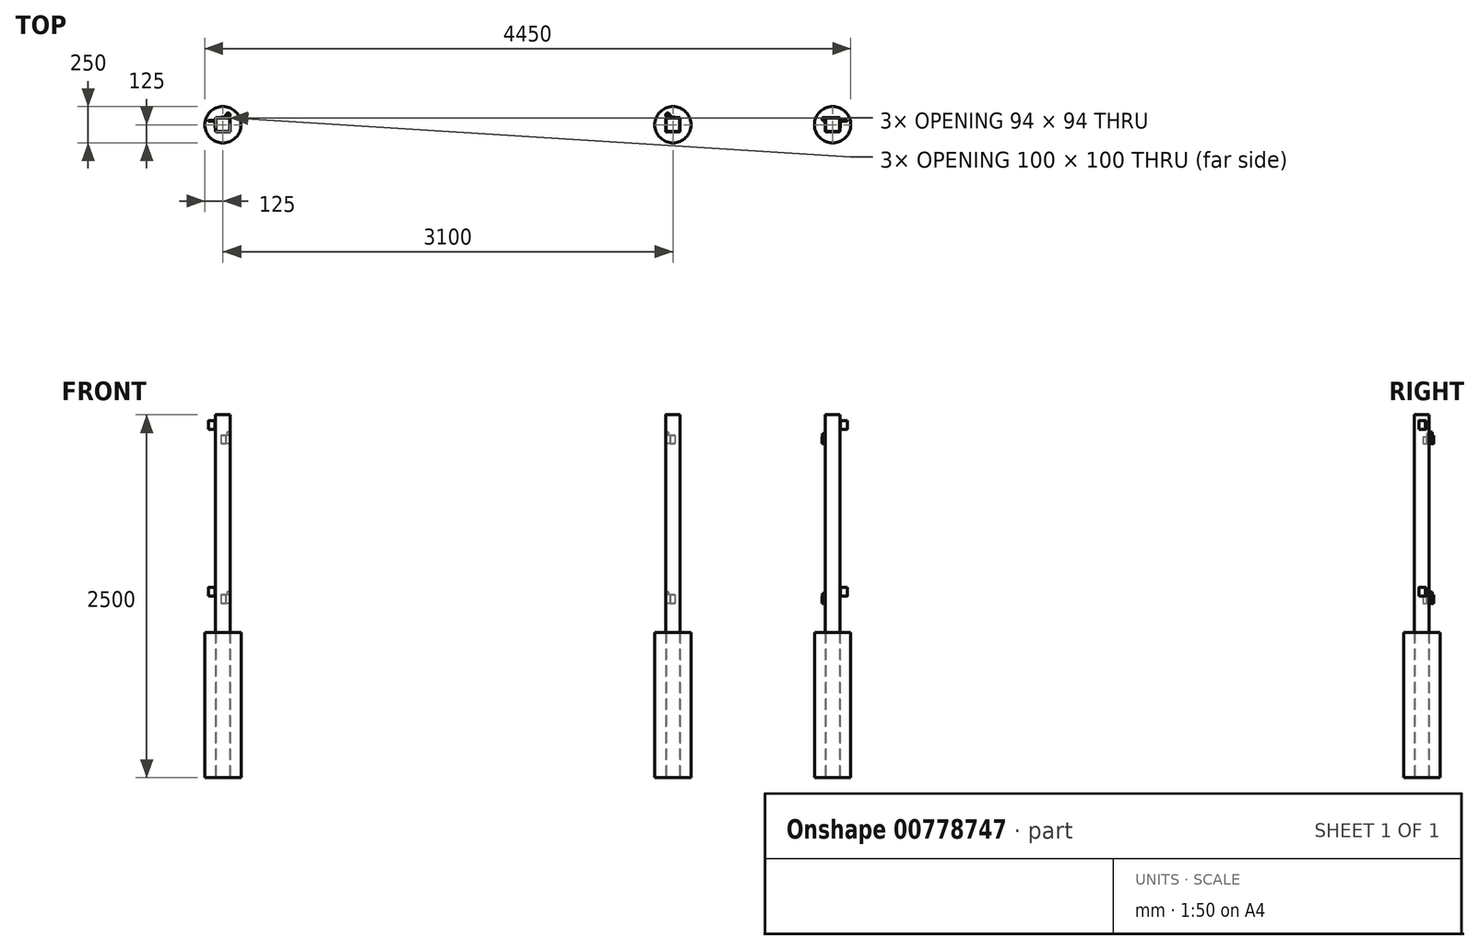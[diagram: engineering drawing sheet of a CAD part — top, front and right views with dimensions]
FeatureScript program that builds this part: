
annotation { "Feature Type Name" : "Feature", "Feature Type Description" : "" }
export const myFeature = defineFeature(function(context is Context, id is Id, definition is map)
    precondition{}
    {
        {
            var Q0;
            Q0=qCreatedBy(makeId("Top.planeOp"),FACE);
            cPlane(context, id + "F0", {"entities" : qUnion([Q0]), "cplaneType" : CPlaneType.OFFSET, "offset" : 1000 * mm, "oppositeDirection" : true, "width" : 150 * mm, "height" : 150 * mm});
        }
        {
            var Q0;
            Q0=qCreatedBy(id+"F0.planeOp",FACE);
            var sketch = newSketch(context, id + "F1", { "sketchPlane" : qUnion([Q0])});
            skLineSegment(sketch, "E0.bottom", {"start": v(-1594, 50) * mm, "end": v(-1506, 50) * mm});
            skLineSegment(sketch, "E0.top", {"start": v(-1594, -50) * mm, "end": v(-1506, -50) * mm});
            skLineSegment(sketch, "E0.left", {"start": v(-1600, 44) * mm, "end": v(-1600, -44) * mm});
            skLineSegment(sketch, "E0.right", {"start": v(-1500, 44) * mm, "end": v(-1500, -44) * mm});
            skLineSegment(sketch, "E1.bottom", {"start": v(1506, 50) * mm, "end": v(1594, 50) * mm});
            skLineSegment(sketch, "E1.top", {"start": v(1506, -50) * mm, "end": v(1594, -50) * mm});
            skLineSegment(sketch, "E1.left", {"start": v(1500, 44) * mm, "end": v(1500, -44) * mm});
            skLineSegment(sketch, "E1.right", {"start": v(1600, 44) * mm, "end": v(1600, -44) * mm});
            skLineSegment(sketch, "E2.bottom", {"start": v(2606, 50) * mm, "end": v(2694, 50) * mm});
            skLineSegment(sketch, "E2.top", {"start": v(2606, -50) * mm, "end": v(2694, -50) * mm});
            skLineSegment(sketch, "E2.left", {"start": v(2600, 44) * mm, "end": v(2600, -44) * mm});
            skLineSegment(sketch, "E2.right", {"start": v(2700, 44) * mm, "end": v(2700, -44) * mm});
            skPoint(sketch, "E3.visualSharp", {"position": v(-1600, 50) * mm});
            skArc(sketch, "E3.filletArc", {"start": v(-1594, 50) * mm, "mid": v(-1598.24, 48.24) * mm, "end": v(-1600, 44) * mm});
            skPoint(sketch, "E4.visualSharp", {"position": v(-1500, 50) * mm});
            skArc(sketch, "E4.filletArc", {"start": v(-1500, 44) * mm, "mid": v(-1501.76, 48.24) * mm, "end": v(-1506, 50) * mm});
            skPoint(sketch, "E5.visualSharp", {"position": v(-1500, -50) * mm});
            skArc(sketch, "E5.filletArc", {"start": v(-1506, -50) * mm, "mid": v(-1501.76, -48.24) * mm, "end": v(-1500, -44) * mm});
            skPoint(sketch, "E6.visualSharp", {"position": v(-1600, -50) * mm});
            skArc(sketch, "E6.filletArc", {"start": v(-1600, -44) * mm, "mid": v(-1598.24, -48.24) * mm, "end": v(-1594, -50) * mm});
            skPoint(sketch, "E7.visualSharp", {"position": v(1500, 50) * mm});
            skArc(sketch, "E7.filletArc", {"start": v(1506, 50) * mm, "mid": v(1501.76, 48.24) * mm, "end": v(1500, 44) * mm});
            skPoint(sketch, "E8.visualSharp", {"position": v(1600, 50) * mm});
            skArc(sketch, "E8.filletArc", {"start": v(1600, 44) * mm, "mid": v(1598.24, 48.24) * mm, "end": v(1594, 50) * mm});
            skPoint(sketch, "E9.visualSharp", {"position": v(1600, -50) * mm});
            skArc(sketch, "E9.filletArc", {"start": v(1594, -50) * mm, "mid": v(1598.24, -48.24) * mm, "end": v(1600, -44) * mm});
            skPoint(sketch, "E10.visualSharp", {"position": v(1500, -50) * mm});
            skArc(sketch, "E10.filletArc", {"start": v(1500, -44) * mm, "mid": v(1501.76, -48.24) * mm, "end": v(1506, -50) * mm});
            skPoint(sketch, "E11.visualSharp", {"position": v(2600, 50) * mm});
            skArc(sketch, "E11.filletArc", {"start": v(2606, 50) * mm, "mid": v(2601.76, 48.24) * mm, "end": v(2600, 44) * mm});
            skPoint(sketch, "E12.visualSharp", {"position": v(2700, 50) * mm});
            skArc(sketch, "E12.filletArc", {"start": v(2700, 44) * mm, "mid": v(2698.24, 48.24) * mm, "end": v(2694, 50) * mm});
            skPoint(sketch, "E13.visualSharp", {"position": v(2700, -50) * mm});
            skArc(sketch, "E13.filletArc", {"start": v(2694, -50) * mm, "mid": v(2698.24, -48.24) * mm, "end": v(2700, -44) * mm});
            skPoint(sketch, "E14.visualSharp", {"position": v(2600, -50) * mm});
            skArc(sketch, "E14.filletArc", {"start": v(2600, -44) * mm, "mid": v(2601.76, -48.24) * mm, "end": v(2606, -50) * mm});
            skArc(sketch, "E15.0", {"start": v(-1594, 47) * mm, "mid": v(-1596.12, 46.12) * mm, "end": v(-1597, 44) * mm});
            skLineSegment(sketch, "E15.1", {"start": v(-1594, 47) * mm, "end": v(-1506, 47) * mm});
            skLineSegment(sketch, "E15.2", {"start": v(-1597, 44) * mm, "end": v(-1597, -44) * mm});
            skArc(sketch, "E15.3", {"start": v(-1503, 44) * mm, "mid": v(-1503.88, 46.12) * mm, "end": v(-1506, 47) * mm});
            skArc(sketch, "E15.4", {"start": v(-1597, -44) * mm, "mid": v(-1596.12, -46.12) * mm, "end": v(-1594, -47) * mm});
            skLineSegment(sketch, "E15.5", {"start": v(-1594, -47) * mm, "end": v(-1506, -47) * mm});
            skArc(sketch, "E15.6", {"start": v(-1506, -47) * mm, "mid": v(-1503.88, -46.12) * mm, "end": v(-1503, -44) * mm});
            skLineSegment(sketch, "E15.7", {"start": v(-1503, 44) * mm, "end": v(-1503, -44) * mm});
            skArc(sketch, "E16.0", {"start": v(1506, 47) * mm, "mid": v(1503.88, 46.12) * mm, "end": v(1503, 44) * mm});
            skLineSegment(sketch, "E16.1", {"start": v(1506, 47) * mm, "end": v(1594, 47) * mm});
            skLineSegment(sketch, "E16.2", {"start": v(1503, 44) * mm, "end": v(1503, -44) * mm});
            skArc(sketch, "E16.3", {"start": v(1597, 44) * mm, "mid": v(1596.12, 46.12) * mm, "end": v(1594, 47) * mm});
            skArc(sketch, "E16.4", {"start": v(1503, -44) * mm, "mid": v(1503.88, -46.12) * mm, "end": v(1506, -47) * mm});
            skLineSegment(sketch, "E16.5", {"start": v(1506, -47) * mm, "end": v(1594, -47) * mm});
            skArc(sketch, "E16.6", {"start": v(1594, -47) * mm, "mid": v(1596.12, -46.12) * mm, "end": v(1597, -44) * mm});
            skLineSegment(sketch, "E16.7", {"start": v(1597, 44) * mm, "end": v(1597, -44) * mm});
            skArc(sketch, "E17.0", {"start": v(2606, 47) * mm, "mid": v(2603.88, 46.12) * mm, "end": v(2603, 44) * mm});
            skLineSegment(sketch, "E17.1", {"start": v(2606, 47) * mm, "end": v(2694, 47) * mm});
            skLineSegment(sketch, "E17.2", {"start": v(2603, 44) * mm, "end": v(2603, -44) * mm});
            skArc(sketch, "E17.3", {"start": v(2697, 44) * mm, "mid": v(2696.12, 46.12) * mm, "end": v(2694, 47) * mm});
            skArc(sketch, "E17.4", {"start": v(2603, -44) * mm, "mid": v(2603.88, -46.12) * mm, "end": v(2606, -47) * mm});
            skLineSegment(sketch, "E17.5", {"start": v(2606, -47) * mm, "end": v(2694, -47) * mm});
            skArc(sketch, "E17.6", {"start": v(2694, -47) * mm, "mid": v(2696.12, -46.12) * mm, "end": v(2697, -44) * mm});
            skLineSegment(sketch, "E17.7", {"start": v(2697, 44) * mm, "end": v(2697, -44) * mm});
            skCircle(sketch, "E18", {"center": v(-1550, 0) * mm, "radius": 125 * mm});
            skPoint(sketch, "E18.centerSnap0", {"position": v(-1550, 47) * mm});
            skPoint(sketch, "E18.centerSnap1", {"position": v(-1500, 0) * mm});
            skCircle(sketch, "E19", {"center": v(1550, 0) * mm, "radius": 125 * mm});
            skPoint(sketch, "E19.centerSnap0", {"position": v(1597, 0) * mm});
            skPoint(sketch, "E19.centerSnap1", {"position": v(1550, 47) * mm});
            skCircle(sketch, "E20", {"center": v(2650, 0) * mm, "radius": 125 * mm});
            skPoint(sketch, "E20.centerSnap0", {"position": v(2697, 0) * mm});
            skPoint(sketch, "E20.centerSnap1", {"position": v(2650, 47) * mm});
            skSolve(sketch);
        }
        {
            var Q0;
            Q0=makeQuery(id+"F1.imprint","IMPRINT",FACE,{"disambiguationData":[TD([[makeQuery(id+"F1.imprint","IMPRINT",EDGE,{"derivedFrom":sQuery(id+"F1.wireOp",EDGE,"E0.bottom")}),-1.0]])]});
            var Q1;
            Q1=makeQuery(id+"F1.imprint","IMPRINT",FACE,{"disambiguationData":[TD([[makeQuery(id+"F1.imprint","IMPRINT",EDGE,{"derivedFrom":sQuery(id+"F1.wireOp",EDGE,"E1.bottom")}),-1.0]])]});
            var Q2;
            Q2=makeQuery(id+"F1.imprint","IMPRINT",FACE,{"disambiguationData":[TD([[makeQuery(id+"F1.imprint","IMPRINT",EDGE,{"derivedFrom":sQuery(id+"F1.wireOp",EDGE,"E2.bottom")}),-1.0]])]});
            extrude(context, id + "F2", {"entities" : qUnion([Q0, Q1, Q2]), "depth" : 2500 * mm, "offsetDistance" : 25 * mm});
        }
        {
            var Q0;
            Q0=makeQuery(id+"F1.imprint","IMPRINT",FACE,{"disambiguationData":[TD([[makeQuery(id+"F1.imprint","IMPRINT",EDGE,{"derivedFrom":sQuery(id+"F1.wireOp",EDGE,"E0.bottom")}),1.0]])]});
            var Q1;
            Q1=makeQuery(id+"F1.imprint","IMPRINT",FACE,{"disambiguationData":[TD([[makeQuery(id+"F1.imprint","IMPRINT",EDGE,{"derivedFrom":sQuery(id+"F1.wireOp",EDGE,"E1.bottom")}),1.0]])]});
            var Q2;
            Q2=makeQuery(id+"F1.imprint","IMPRINT",FACE,{"disambiguationData":[TD([[makeQuery(id+"F1.imprint","IMPRINT",EDGE,{"derivedFrom":sQuery(id+"F1.wireOp",EDGE,"E2.bottom")}),1.0]])]});
            extrude(context, id + "F3", {"entities" : qUnion([Q0, Q1, Q2]), "depth" : 1000 * mm, "offsetDistance" : 25 * mm});
        }
        {
            var Q0;
            Q0=qCreatedBy(makeId("Top.planeOp"),FACE);
            cPlane(context, id + "F4", {"entities" : qUnion([Q0]), "cplaneType" : CPlaneType.OFFSET, "offset" : 200 * mm, "width" : 150 * mm, "height" : 150 * mm});
        }
        {
            var Q0;
            Q0=qCreatedBy(makeId("Top.planeOp"),FACE);
            cPlane(context, id + "F5", {"entities" : qUnion([Q0]), "cplaneType" : CPlaneType.OFFSET, "offset" : 250 * mm, "width" : 150 * mm, "height" : 150 * mm});
        }
        {
            var Q0;
            Q0=qCreatedBy(makeId("Top.planeOp"),FACE);
            cPlane(context, id + "F6", {"entities" : qUnion([Q0]), "cplaneType" : CPlaneType.OFFSET, "offset" : 1400 * mm, "width" : 150 * mm, "height" : 150 * mm});
        }
        {
            var Q0;
            Q0=qCreatedBy(makeId("Top.planeOp"),FACE);
            cPlane(context, id + "F7", {"entities" : qUnion([Q0]), "cplaneType" : CPlaneType.OFFSET, "offset" : 1300 * mm, "width" : 150 * mm, "height" : 150 * mm});
        }
        {
            var Q0;
            Q0=qCreatedBy(id+"F5.planeOp",FACE);
            var sketch = newSketch(context, id + "F8", { "sketchPlane" : qUnion([Q0])});
            skLineSegment(sketch, "E21", {"start": v(-1600, 29) * mm, "end": v(-1600, -19) * mm});
            skLineSegment(sketch, "E22", {"start": v(-1601, -20) * mm, "end": v(-1602, -20) * mm});
            skLineSegment(sketch, "E23", {"start": v(-1605, -17) * mm, "end": v(-1605, 22) * mm});
            skLineSegment(sketch, "E24", {"start": v(-1608, 25) * mm, "end": v(-1647, 25) * mm});
            skLineSegment(sketch, "E25", {"start": v(-1650, 28) * mm, "end": v(-1650, 29) * mm});
            skLineSegment(sketch, "E26", {"start": v(-1649, 30) * mm, "end": v(-1601, 30) * mm});
            skLineSegment(sketch, "E27", {"start": v(2700, 29) * mm, "end": v(2700, -19) * mm});
            skLineSegment(sketch, "E28", {"start": v(2701, -20) * mm, "end": v(2702, -20) * mm});
            skLineSegment(sketch, "E29", {"start": v(2705, -17) * mm, "end": v(2705, 22) * mm});
            skLineSegment(sketch, "E30", {"start": v(2708, 25) * mm, "end": v(2747, 25) * mm});
            skLineSegment(sketch, "E31", {"start": v(2750, 28) * mm, "end": v(2750, 29) * mm});
            skLineSegment(sketch, "E32", {"start": v(2749, 30) * mm, "end": v(2701, 30) * mm});
            skPoint(sketch, "E33.visualSharp", {"position": v(-1650, 30) * mm});
            skArc(sketch, "E33.filletArc", {"start": v(-1649, 30) * mm, "mid": v(-1649.7, 29.7) * mm, "end": v(-1650, 29) * mm});
            skPoint(sketch, "E34.visualSharp", {"position": v(-1650, 25) * mm});
            skArc(sketch, "E34.filletArc", {"start": v(-1650, 28) * mm, "mid": v(-1649.12, 25.88) * mm, "end": v(-1647, 25) * mm});
            skPoint(sketch, "E35.visualSharp", {"position": v(-1600, 30) * mm});
            skArc(sketch, "E35.filletArc", {"start": v(-1600, 29) * mm, "mid": v(-1600.3, 29.7) * mm, "end": v(-1601, 30) * mm});
            skPoint(sketch, "E36.visualSharp", {"position": v(-1605, 25) * mm});
            skArc(sketch, "E36.filletArc", {"start": v(-1605, 22) * mm, "mid": v(-1605.88, 24.12) * mm, "end": v(-1608, 25) * mm});
            skPoint(sketch, "E37.visualSharp", {"position": v(-1600, -20) * mm});
            skArc(sketch, "E37.filletArc", {"start": v(-1601, -20) * mm, "mid": v(-1600.3, -19.7) * mm, "end": v(-1600, -19) * mm});
            skPoint(sketch, "E38.visualSharp", {"position": v(-1605, -20) * mm});
            skArc(sketch, "E38.filletArc", {"start": v(-1605, -17) * mm, "mid": v(-1604.12, -19.12) * mm, "end": v(-1602, -20) * mm});
            skPoint(sketch, "E39.visualSharp", {"position": v(2750, 30) * mm});
            skArc(sketch, "E39.filletArc", {"start": v(2750, 29) * mm, "mid": v(2749.7, 29.7) * mm, "end": v(2749, 30) * mm});
            skPoint(sketch, "E40.visualSharp", {"position": v(2750, 25) * mm});
            skArc(sketch, "E40.filletArc", {"start": v(2747, 25) * mm, "mid": v(2749.12, 25.88) * mm, "end": v(2750, 28) * mm});
            skPoint(sketch, "E41.visualSharp", {"position": v(2700, 30) * mm});
            skArc(sketch, "E41.filletArc", {"start": v(2701, 30) * mm, "mid": v(2700.3, 29.7) * mm, "end": v(2700, 29) * mm});
            skPoint(sketch, "E42.visualSharp", {"position": v(2705, 25) * mm});
            skArc(sketch, "E42.filletArc", {"start": v(2708, 25) * mm, "mid": v(2705.88, 24.12) * mm, "end": v(2705, 22) * mm});
            skPoint(sketch, "E43.visualSharp", {"position": v(2700, -20) * mm});
            skArc(sketch, "E43.filletArc", {"start": v(2700, -19) * mm, "mid": v(2700.3, -19.7) * mm, "end": v(2701, -20) * mm});
            skPoint(sketch, "E44.visualSharp", {"position": v(2705, -20) * mm});
            skArc(sketch, "E44.filletArc", {"start": v(2702, -20) * mm, "mid": v(2704.12, -19.12) * mm, "end": v(2705, -17) * mm});
            skSolve(sketch);
        }
        {
            var Q0;
            Q0=makeQuery(id+"F8.imprint","IMPRINT",FACE,{"disambiguationData":[TD([[makeQuery(id+"F8.imprint","IMPRINT",EDGE,{"derivedFrom":sQuery(id+"F8.wireOp",EDGE,"E21")}),-1.0]])]});
            var Q1;
            Q1=makeQuery(id+"F8.imprint","IMPRINT",FACE,{"disambiguationData":[TD([[makeQuery(id+"F8.imprint","IMPRINT",EDGE,{"derivedFrom":sQuery(id+"F8.wireOp",EDGE,"E27")}),1.0]])]});
            extrude(context, id + "F9", {"entities" : qUnion([Q0, Q1]), "depth" : 60 * mm, "offsetDistance" : 25 * mm});
        }
        {
            var Q0;
            Q0=qCreatedBy(id+"F6.planeOp",FACE);
            var sketch = newSketch(context, id + "F10", { "sketchPlane" : qUnion([Q0])});
            skLineSegment(sketch, "E45", {"start": v(-1600, 29) * mm, "end": v(-1600, -19) * mm});
            skLineSegment(sketch, "E46", {"start": v(-1601, -20) * mm, "end": v(-1602, -20) * mm});
            skLineSegment(sketch, "E47", {"start": v(-1605, -17) * mm, "end": v(-1605, 22) * mm});
            skLineSegment(sketch, "E48", {"start": v(-1608, 25) * mm, "end": v(-1647, 25) * mm});
            skLineSegment(sketch, "E49", {"start": v(-1650, 28) * mm, "end": v(-1650, 29) * mm});
            skLineSegment(sketch, "E50", {"start": v(-1649, 30) * mm, "end": v(-1601, 30) * mm});
            skLineSegment(sketch, "E51", {"start": v(2700, 29) * mm, "end": v(2700, -19) * mm});
            skLineSegment(sketch, "E52", {"start": v(2701, -20) * mm, "end": v(2702, -20) * mm});
            skLineSegment(sketch, "E53", {"start": v(2705, -17) * mm, "end": v(2705, 22) * mm});
            skLineSegment(sketch, "E54", {"start": v(2708, 25) * mm, "end": v(2747, 25) * mm});
            skLineSegment(sketch, "E55", {"start": v(2750, 28) * mm, "end": v(2750, 29) * mm});
            skLineSegment(sketch, "E56", {"start": v(2749, 30) * mm, "end": v(2701, 30) * mm});
            skPoint(sketch, "E57.visualSharp", {"position": v(-1650, 30) * mm});
            skArc(sketch, "E57.filletArc", {"start": v(-1649, 30) * mm, "mid": v(-1649.7, 29.7) * mm, "end": v(-1650, 29) * mm});
            skPoint(sketch, "E58.visualSharp", {"position": v(-1650, 25) * mm});
            skArc(sketch, "E58.filletArc", {"start": v(-1650, 28) * mm, "mid": v(-1649.12, 25.88) * mm, "end": v(-1647, 25) * mm});
            skPoint(sketch, "E59.visualSharp", {"position": v(-1600, 30) * mm});
            skArc(sketch, "E59.filletArc", {"start": v(-1600, 29) * mm, "mid": v(-1600.3, 29.7) * mm, "end": v(-1601, 30) * mm});
            skPoint(sketch, "E60.visualSharp", {"position": v(-1605, 25) * mm});
            skArc(sketch, "E60.filletArc", {"start": v(-1605, 22) * mm, "mid": v(-1605.88, 24.12) * mm, "end": v(-1608, 25) * mm});
            skPoint(sketch, "E61.visualSharp", {"position": v(-1600, -20) * mm});
            skArc(sketch, "E61.filletArc", {"start": v(-1601, -20) * mm, "mid": v(-1600.3, -19.7) * mm, "end": v(-1600, -19) * mm});
            skPoint(sketch, "E62.visualSharp", {"position": v(-1605, -20) * mm});
            skArc(sketch, "E62.filletArc", {"start": v(-1605, -17) * mm, "mid": v(-1604.12, -19.12) * mm, "end": v(-1602, -20) * mm});
            skPoint(sketch, "E63.visualSharp", {"position": v(2750, 30) * mm});
            skArc(sketch, "E63.filletArc", {"start": v(2750, 29) * mm, "mid": v(2749.7, 29.7) * mm, "end": v(2749, 30) * mm});
            skPoint(sketch, "E64.visualSharp", {"position": v(2750, 25) * mm});
            skArc(sketch, "E64.filletArc", {"start": v(2747, 25) * mm, "mid": v(2749.12, 25.88) * mm, "end": v(2750, 28) * mm});
            skPoint(sketch, "E65.visualSharp", {"position": v(2700, 30) * mm});
            skArc(sketch, "E65.filletArc", {"start": v(2701, 30) * mm, "mid": v(2700.3, 29.7) * mm, "end": v(2700, 29) * mm});
            skPoint(sketch, "E66.visualSharp", {"position": v(2705, 25) * mm});
            skArc(sketch, "E66.filletArc", {"start": v(2708, 25) * mm, "mid": v(2705.88, 24.12) * mm, "end": v(2705, 22) * mm});
            skPoint(sketch, "E67.visualSharp", {"position": v(2700, -20) * mm});
            skArc(sketch, "E67.filletArc", {"start": v(2700, -19) * mm, "mid": v(2700.3, -19.7) * mm, "end": v(2701, -20) * mm});
            skPoint(sketch, "E68.visualSharp", {"position": v(2705, -20) * mm});
            skArc(sketch, "E68.filletArc", {"start": v(2702, -20) * mm, "mid": v(2704.12, -19.12) * mm, "end": v(2705, -17) * mm});
            skSolve(sketch);
        }
        {
            var Q0;
            Q0=makeQuery(id+"F10.imprint","IMPRINT",FACE,{"disambiguationData":[TD([[makeQuery(id+"F10.imprint","IMPRINT",EDGE,{"derivedFrom":sQuery(id+"F10.wireOp",EDGE,"E45")}),-1.0]])]});
            var Q1;
            Q1=makeQuery(id+"F10.imprint","IMPRINT",FACE,{"disambiguationData":[TD([[makeQuery(id+"F10.imprint","IMPRINT",EDGE,{"derivedFrom":sQuery(id+"F10.wireOp",EDGE,"E51")}),1.0]])]});
            extrude(context, id + "F11", {"entities" : qUnion([Q0, Q1]), "depth" : 60 * mm, "offsetDistance" : 25 * mm});
        }
        {
            var Q0;
            Q0=qCreatedBy(id+"F4.planeOp",FACE);
            var sketch = newSketch(context, id + "F12", { "sketchPlane" : qUnion([Q0])});
            skLineSegment(sketch, "E69", {"start": v(-1529, 50) * mm, "end": v(-1562, 50) * mm});
            skLineSegment(sketch, "E70", {"start": v(-1563, 51) * mm, "end": v(-1563, 52) * mm});
            skLineSegment(sketch, "E71", {"start": v(-1561, 54) * mm, "end": v(-1534, 54) * mm});
            skLineSegment(sketch, "E72", {"start": v(-1532, 56) * mm, "end": v(-1532, 70) * mm});
            skLineSegment(sketch, "E73", {"start": v(-1532, 70) * mm, "end": v(-1528, 70) * mm});
            skLineSegment(sketch, "E74", {"start": v(-1528, 70) * mm, "end": v(-1528, 51) * mm});
            skCircle(sketch, "E75", {"center": v(-1514, 67) * mm, "radius": 14 * mm});
            skPoint(sketch, "E76.visualSharp", {"position": v(-1563, 50) * mm});
            skArc(sketch, "E76.filletArc", {"start": v(-1563, 51) * mm, "mid": v(-1562.7, 50.3) * mm, "end": v(-1562, 50) * mm});
            skPoint(sketch, "E77.visualSharp", {"position": v(-1563, 54) * mm});
            skArc(sketch, "E77.filletArc", {"start": v(-1561, 54) * mm, "mid": v(-1562.41, 53.41) * mm, "end": v(-1563, 52) * mm});
            skPoint(sketch, "E78.visualSharp", {"position": v(-1532, 54) * mm});
            skArc(sketch, "E78.filletArc", {"start": v(-1534, 54) * mm, "mid": v(-1532.59, 54.59) * mm, "end": v(-1532, 56) * mm});
            skPoint(sketch, "E79.visualSharp", {"position": v(-1528, 50) * mm});
            skArc(sketch, "E79.filletArc", {"start": v(-1529, 50) * mm, "mid": v(-1528.3, 50.3) * mm, "end": v(-1528, 51) * mm});
            skCircle(sketch, "E80", {"center": v(-1514, 67) * mm, "radius": 7 * mm});
            skLineSegment(sketch, "E81", {"start": v(1529, 50) * mm, "end": v(1562, 50) * mm});
            skLineSegment(sketch, "E82", {"start": v(1563, 51) * mm, "end": v(1563, 52) * mm});
            skLineSegment(sketch, "E83", {"start": v(1561, 54) * mm, "end": v(1534, 54) * mm});
            skLineSegment(sketch, "E84", {"start": v(1532, 56) * mm, "end": v(1532, 70) * mm});
            skLineSegment(sketch, "E85", {"start": v(1532, 70) * mm, "end": v(1528, 70) * mm});
            skLineSegment(sketch, "E86", {"start": v(1528, 70) * mm, "end": v(1528, 51) * mm});
            skCircle(sketch, "E87", {"center": v(1514, 67) * mm, "radius": 14 * mm});
            skCircle(sketch, "E88", {"center": v(1514, 67) * mm, "radius": 7 * mm});
            skPoint(sketch, "E89.visualSharp", {"position": v(1528, 50) * mm});
            skArc(sketch, "E89.filletArc", {"start": v(1528, 51) * mm, "mid": v(1528.3, 50.3) * mm, "end": v(1529, 50) * mm});
            skPoint(sketch, "E90.visualSharp", {"position": v(1532, 54) * mm});
            skArc(sketch, "E90.filletArc", {"start": v(1532, 56) * mm, "mid": v(1532.59, 54.59) * mm, "end": v(1534, 54) * mm});
            skPoint(sketch, "E91.visualSharp", {"position": v(1563, 54) * mm});
            skArc(sketch, "E91.filletArc", {"start": v(1563, 52) * mm, "mid": v(1562.41, 53.41) * mm, "end": v(1561, 54) * mm});
            skPoint(sketch, "E92.visualSharp", {"position": v(1563, 50) * mm});
            skArc(sketch, "E92.filletArc", {"start": v(1562, 50) * mm, "mid": v(1562.7, 50.3) * mm, "end": v(1563, 51) * mm});
            skLineSegment(sketch, "E93", {"start": v(2600, 50) * mm, "end": v(2600, 10) * mm});
            skLineSegment(sketch, "E94", {"start": v(2600, 10) * mm, "end": v(2596, 10) * mm});
            skLineSegment(sketch, "E95", {"start": v(2596, 10) * mm, "end": v(2596, 50) * mm});
            skLineSegment(sketch, "E96", {"start": v(2596, 50) * mm, "end": v(2600, 50) * mm});
            skCircle(sketch, "E97", {"center": v(2586, 40) * mm, "radius": 10 * mm});
            skCircle(sketch, "E98", {"center": v(2586, 40) * mm, "radius": 7 * mm});
            skSolve(sketch);
        }
        {
            var Q0;
            Q0=makeQuery(id+"F12.imprint","IMPRINT",FACE,{"disambiguationData":[TD([[makeQuery(id+"F12.imprint","IMPRINT",EDGE,{"derivedFrom":sQuery(id+"F12.wireOp",EDGE,"E69")}),-1.0]])]});
            var Q1;
            Q1=makeQuery(id+"F12.imprint","IMPRINT",FACE,{"disambiguationData":[TD([[makeQuery(id+"F12.imprint","IMPRINT",EDGE,{"derivedFrom":sQuery(id+"F12.wireOp",EDGE,"E81")}),1.0]])]});
            extrude(context, id + "F13", {"entities" : qUnion([Q0, Q1]), "depth" : 60 * mm, "offsetDistance" : 25 * mm});
        }
        {
            var Q0;
            Q0=qCreatedBy(id+"F7.planeOp",FACE);
            var sketch = newSketch(context, id + "F14", { "sketchPlane" : qUnion([Q0])});
            skLineSegment(sketch, "E99", {"start": v(-1529, 50) * mm, "end": v(-1562, 50) * mm});
            skLineSegment(sketch, "E100", {"start": v(-1563, 51) * mm, "end": v(-1563, 52) * mm});
            skLineSegment(sketch, "E101", {"start": v(-1561, 54) * mm, "end": v(-1534, 54) * mm});
            skLineSegment(sketch, "E102", {"start": v(-1532, 56) * mm, "end": v(-1532, 70) * mm});
            skLineSegment(sketch, "E103", {"start": v(-1532, 70) * mm, "end": v(-1528, 70) * mm});
            skLineSegment(sketch, "E104", {"start": v(-1528, 70) * mm, "end": v(-1528, 51) * mm});
            skCircle(sketch, "E105", {"center": v(-1514, 67) * mm, "radius": 14 * mm});
            skPoint(sketch, "E106.visualSharp", {"position": v(-1563, 50) * mm});
            skArc(sketch, "E106.filletArc", {"start": v(-1563, 51) * mm, "mid": v(-1562.7, 50.3) * mm, "end": v(-1562, 50) * mm});
            skPoint(sketch, "E107.visualSharp", {"position": v(-1563, 54) * mm});
            skArc(sketch, "E107.filletArc", {"start": v(-1561, 54) * mm, "mid": v(-1562.41, 53.41) * mm, "end": v(-1563, 52) * mm});
            skPoint(sketch, "E108.visualSharp", {"position": v(-1532, 54) * mm});
            skArc(sketch, "E108.filletArc", {"start": v(-1534, 54) * mm, "mid": v(-1532.59, 54.59) * mm, "end": v(-1532, 56) * mm});
            skPoint(sketch, "E109.visualSharp", {"position": v(-1528, 50) * mm});
            skArc(sketch, "E109.filletArc", {"start": v(-1529, 50) * mm, "mid": v(-1528.3, 50.3) * mm, "end": v(-1528, 51) * mm});
            skCircle(sketch, "E110", {"center": v(-1514, 67) * mm, "radius": 7 * mm});
            skLineSegment(sketch, "E111", {"start": v(1529, 50) * mm, "end": v(1562, 50) * mm});
            skLineSegment(sketch, "E112", {"start": v(1563, 51) * mm, "end": v(1563, 52) * mm});
            skLineSegment(sketch, "E113", {"start": v(1561, 54) * mm, "end": v(1534, 54) * mm});
            skLineSegment(sketch, "E114", {"start": v(1532, 56) * mm, "end": v(1532, 70) * mm});
            skLineSegment(sketch, "E115", {"start": v(1532, 70) * mm, "end": v(1528, 70) * mm});
            skLineSegment(sketch, "E116", {"start": v(1528, 70) * mm, "end": v(1528, 51) * mm});
            skCircle(sketch, "E117", {"center": v(1514, 67) * mm, "radius": 14 * mm});
            skCircle(sketch, "E118", {"center": v(1514, 67) * mm, "radius": 7 * mm});
            skPoint(sketch, "E119.visualSharp", {"position": v(1528, 50) * mm});
            skArc(sketch, "E119.filletArc", {"start": v(1528, 51) * mm, "mid": v(1528.3, 50.3) * mm, "end": v(1529, 50) * mm});
            skPoint(sketch, "E120.visualSharp", {"position": v(1532, 54) * mm});
            skArc(sketch, "E120.filletArc", {"start": v(1532, 56) * mm, "mid": v(1532.59, 54.59) * mm, "end": v(1534, 54) * mm});
            skPoint(sketch, "E121.visualSharp", {"position": v(1563, 54) * mm});
            skArc(sketch, "E121.filletArc", {"start": v(1563, 52) * mm, "mid": v(1562.41, 53.41) * mm, "end": v(1561, 54) * mm});
            skPoint(sketch, "E122.visualSharp", {"position": v(1563, 50) * mm});
            skArc(sketch, "E122.filletArc", {"start": v(1562, 50) * mm, "mid": v(1562.7, 50.3) * mm, "end": v(1563, 51) * mm});
            skLineSegment(sketch, "E123", {"start": v(2600, 50) * mm, "end": v(2600, 10) * mm});
            skLineSegment(sketch, "E124", {"start": v(2600, 10) * mm, "end": v(2596, 10) * mm});
            skLineSegment(sketch, "E125", {"start": v(2596, 10) * mm, "end": v(2596, 50) * mm});
            skLineSegment(sketch, "E126", {"start": v(2596, 50) * mm, "end": v(2600, 50) * mm});
            skCircle(sketch, "E127", {"center": v(2586, 40) * mm, "radius": 10 * mm});
            skCircle(sketch, "E128", {"center": v(2586, 40) * mm, "radius": 7 * mm});
            skSolve(sketch);
        }
        {
            var Q0;
            Q0=makeQuery(id+"F14.imprint","IMPRINT",FACE,{"disambiguationData":[TD([[makeQuery(id+"F14.imprint","IMPRINT",EDGE,{"derivedFrom":sQuery(id+"F14.wireOp",EDGE,"E111")}),1.0]])]});
            var Q1;
            Q1=makeQuery(id+"F14.imprint","IMPRINT",FACE,{"disambiguationData":[TD([[makeQuery(id+"F14.imprint","IMPRINT",EDGE,{"derivedFrom":sQuery(id+"F14.wireOp",EDGE,"E99")}),-1.0]])]});
            extrude(context, id + "F15", {"entities" : qUnion([Q0, Q1]), "depth" : 60 * mm, "offsetDistance" : 25 * mm});
        }
        {
            var Q0;
            Q0=makeQuery(id+"F12.imprint","IMPRINT",FACE,{"disambiguationData":[TD([[makeQuery(id+"F12.imprint","IMPRINT",EDGE,{"derivedFrom":sQuery(id+"F12.wireOp",EDGE,"E75")}),1.0]])]});
            var Q1;
            Q1=makeQuery(id+"F12.imprint","IMPRINT",FACE,{"disambiguationData":[TD([[makeQuery(id+"F12.imprint","IMPRINT",EDGE,{"derivedFrom":sQuery(id+"F12.wireOp",EDGE,"E87")}),1.0]])]});
            extrude(context, id + "F16", {"entities" : qUnion([Q0, Q1]), "depth" : 60 * mm, "offsetDistance" : 25 * mm});
        }
        {
            var Q0;
            Q0=makeQuery(id+"F12.imprint","IMPRINT",FACE,{"disambiguationData":[TD([[makeQuery(id+"F12.imprint","IMPRINT",EDGE,{"derivedFrom":sQuery(id+"F12.wireOp",EDGE,"E80")}),1.0]])]});
            var Q1;
            Q1=makeQuery(id+"F12.imprint","IMPRINT",FACE,{"disambiguationData":[TD([[makeQuery(id+"F12.imprint","IMPRINT",EDGE,{"derivedFrom":sQuery(id+"F12.wireOp",EDGE,"E88")}),1.0]])]});
            extrude(context, id + "F17", {"entities" : qUnion([Q0, Q1]), "operationType" : NewBodyOperationType.ADD, "depth" : 80 * mm, "offsetDistance" : 25 * mm});
        }
        {
            var Q0;
            Q0=makeQuery(id+"F14.imprint","IMPRINT",FACE,{"disambiguationData":[TD([[makeQuery(id+"F14.imprint","IMPRINT",EDGE,{"derivedFrom":sQuery(id+"F14.wireOp",EDGE,"E105")}),1.0]])]});
            var Q1;
            Q1=makeQuery(id+"F14.imprint","IMPRINT",FACE,{"disambiguationData":[TD([[makeQuery(id+"F14.imprint","IMPRINT",EDGE,{"derivedFrom":sQuery(id+"F14.wireOp",EDGE,"E117")}),1.0]])]});
            extrude(context, id + "F18", {"entities" : qUnion([Q0, Q1]), "depth" : 60 * mm, "offsetDistance" : 25 * mm});
        }
        {
            var Q0;
            Q0=makeQuery(id+"F14.imprint","IMPRINT",FACE,{"disambiguationData":[TD([[makeQuery(id+"F14.imprint","IMPRINT",EDGE,{"derivedFrom":sQuery(id+"F14.wireOp",EDGE,"E110")}),1.0]])]});
            var Q1;
            Q1=makeQuery(id+"F14.imprint","IMPRINT",FACE,{"disambiguationData":[TD([[makeQuery(id+"F14.imprint","IMPRINT",EDGE,{"derivedFrom":sQuery(id+"F14.wireOp",EDGE,"E118")}),1.0]])]});
            extrude(context, id + "F19", {"entities" : qUnion([Q0, Q1]), "operationType" : NewBodyOperationType.ADD, "depth" : 80 * mm, "offsetDistance" : 25 * mm});
        }
        {
            var Q0;
            Q0=makeQuery(id+"F12.imprint","IMPRINT",FACE,{"disambiguationData":[TD([[makeQuery(id+"F12.imprint","IMPRINT",EDGE,{"derivedFrom":sQuery(id+"F12.wireOp",EDGE,"E93")}),-1.0]])]});
            extrude(context, id + "F20", {"entities" : qUnion([Q0]), "depth" : 50 * mm, "offsetDistance" : 25 * mm});
        }
        {
            var Q0;
            Q0=makeQuery(id+"F12.imprint","IMPRINT",FACE,{"disambiguationData":[TD([[makeQuery(id+"F12.imprint","IMPRINT",EDGE,{"derivedFrom":sQuery(id+"F12.wireOp",EDGE,"E97")}),1.0]])]});
            var Q1;
            Q1=makeQuery(id+"F12.imprint","IMPRINT",FACE,{"disambiguationData":[TD([[makeQuery(id+"F12.imprint","IMPRINT",EDGE,{"derivedFrom":sQuery(id+"F12.wireOp",EDGE,"E98")}),1.0]])]});
            extrude(context, id + "F21", {"entities" : qUnion([Q0, Q1]), "operationType" : NewBodyOperationType.ADD, "depth" : 50 * mm, "offsetDistance" : 25 * mm});
        }
        {
            var Q0;
            Q0=makeQuery(id+"F12.imprint","IMPRINT",FACE,{"disambiguationData":[TD([[makeQuery(id+"F12.imprint","IMPRINT",EDGE,{"derivedFrom":sQuery(id+"F12.wireOp",EDGE,"E98")}),1.0]])]});
            extrude(context, id + "F22", {"entities" : qUnion([Q0]), "operationType" : NewBodyOperationType.ADD, "depth" : 70 * mm, "offsetDistance" : 25 * mm});
        }
        {
            var Q0;
            Q0=makeQuery(id+"F14.imprint","IMPRINT",FACE,{"disambiguationData":[TD([[makeQuery(id+"F14.imprint","IMPRINT",EDGE,{"derivedFrom":sQuery(id+"F14.wireOp",EDGE,"E123")}),-1.0]])]});
            extrude(context, id + "F23", {"entities" : qUnion([Q0]), "depth" : 50 * mm, "offsetDistance" : 25 * mm});
        }
        {
            var Q0;
            Q0=makeQuery(id+"F14.imprint","IMPRINT",FACE,{"disambiguationData":[TD([[makeQuery(id+"F14.imprint","IMPRINT",EDGE,{"derivedFrom":sQuery(id+"F14.wireOp",EDGE,"E127")}),1.0]])]});
            extrude(context, id + "F24", {"entities" : qUnion([Q0]), "depth" : 50 * mm, "offsetDistance" : 25 * mm});
        }
        {
            var Q0;
            Q0=makeQuery(id+"F14.imprint","IMPRINT",FACE,{"disambiguationData":[TD([[makeQuery(id+"F14.imprint","IMPRINT",EDGE,{"derivedFrom":sQuery(id+"F14.wireOp",EDGE,"E128")}),1.0]])]});
            extrude(context, id + "F25", {"entities" : qUnion([Q0]), "operationType" : NewBodyOperationType.ADD, "depth" : 70 * mm, "offsetDistance" : 25 * mm});
        }
    });
